# Revit family: Eurolan_Вентиляторная панель 19 1U с контроллером
name_source: partatom
category: Устройства связи
units: mm (PartAtom-declared; Revit-internal decimal feet)

## family parameters
Всегда вертикально = Да
На основе рабочей плоскости = Нет
Общий = Нет
При загрузке вырезать с полостями = Нет
Размер круглого соединителя = Использовать диаметр
Сохранять ориентацию аннотаций = Нет
Тип детали = Нормальный
Точка расчета площади = Нет

## types (2) — shared parameters
ADSK_Единица измерения = шт
ADSK_Завод-изготовитель = Eurolan
ADSK_Количество = 1
ADSK_Марка = 1U
ADSK_Материал = RAL 9005
ADSK_Наименование краткое = Вентиляторная панель 19" 1U

## per-type parameters (varying)
| type | ADSK_Код изделия | ADSK_Масса | ADSK_Наименование | Выбор_геометрии |
| Вентиляторная панель 19" 1U_3 вентилятора | 60A-91-10-30BL | 4.5 | Вентиляторная панель 19" 1U, 3 вентилятора, с контроллером | Вентиляторная панель 19 1U 3 вентилятора |
| Вентиляторная панель 19" 1U_6 вентиляторов | 60A-91-11-30BL | 8.5 | Вентиляторная панель 19" 1U, 6 вентиляторов, с контроллером | Вентиляторная панель 19 1U 6 вентиляторов |
